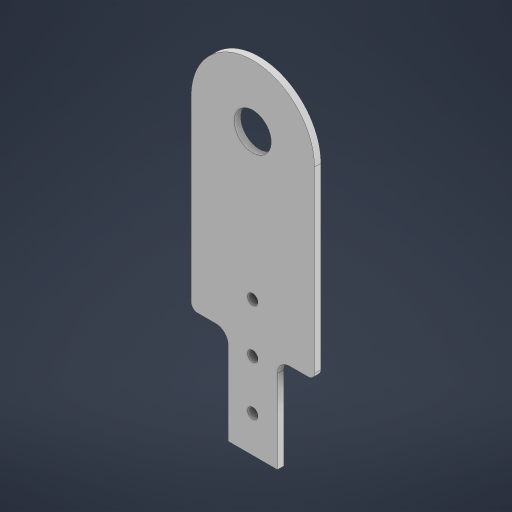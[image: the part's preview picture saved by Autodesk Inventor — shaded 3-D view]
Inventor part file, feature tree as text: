
AUTODESK INVENTOR PART (.ipt)
format: ipt  version: 2024 (Build 280153000, 153)  size: 214,528 bytes
history: native  units: in
note: dims shown in document units (in); Inventor stores cm internally (conversion verified against a paired STEP export)
features: fillet x5, other x1, extrude x1, sketch x1
ambient origin geometry x8: Origin, YZ Plane, XZ Plane, XY Plane, X Axis, Y Axis, Z Axis, Center Point
bodies: Solid1 (feature_tree)
feature tree (8):
  other  "Wrist plate"
  extrude  "Extrusion1"  Depth=5.0in
  fillet  "Fillet1"  Radius=0.748in
  fillet  "Fillet2"  Radius=0.209in
  fillet  "Fillet3"  Radius=0.209in
  fillet  "Fillet4"  Radius=1.25in
  fillet  "Fillet5"  Radius=4.2in
  sketch  "Sketch1"  dims[d0=2.5in d1=5.0in d2=0.748in d3=0.209in d4=0.209in d5=1.25in d6=4.2in d8=0.13in d9=0.0in d10=1.25in d11=1.25in d12=0.125in d13=0.125in d14=1.0in d15=1.0in d16=3.5in d17=1.0in d18=0.25in]
